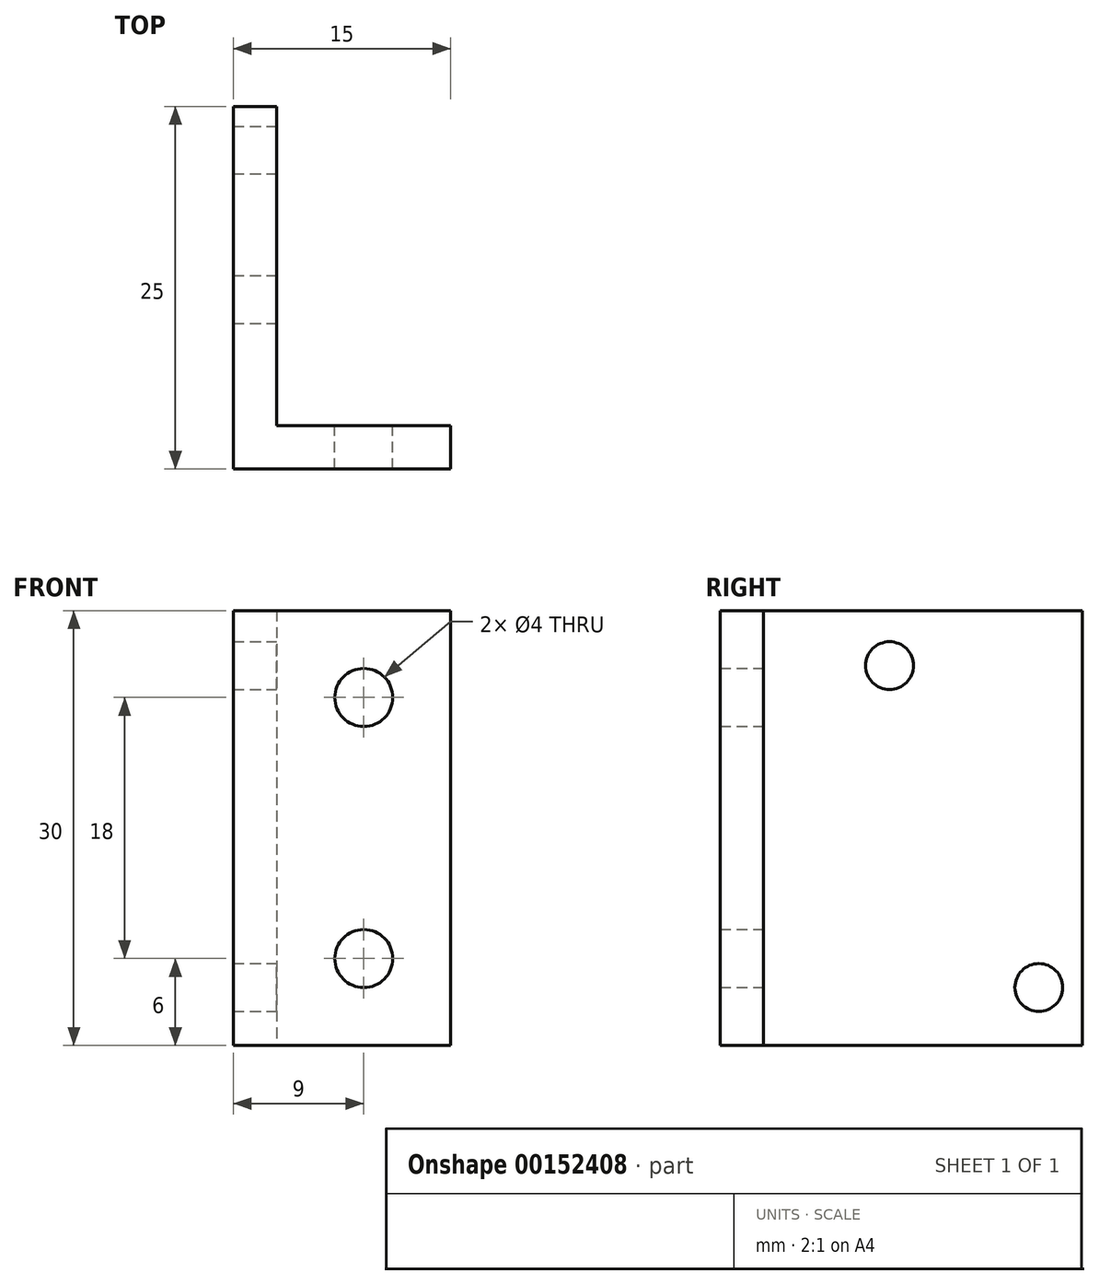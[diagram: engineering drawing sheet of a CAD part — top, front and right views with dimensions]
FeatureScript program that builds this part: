
annotation { "Feature Type Name" : "Feature", "Feature Type Description" : "" }
export const myFeature = defineFeature(function(context is Context, id is Id, definition is map)
    precondition{}
    {
        {
            var Q0;
            Q0=qCreatedBy(makeId("Top.planeOp"),FACE);
            var sketch = newSketch(context, id + "F0", { "sketchPlane" : qUnion([Q0])});
            skLineSegment(sketch, "E0", {"start": v(0, 0) * mm, "end": v(15, 0) * mm});
            skLineSegment(sketch, "E1", {"start": v(15, 0) * mm, "end": v(15, 3) * mm});
            skLineSegment(sketch, "E2", {"start": v(15, 3) * mm, "end": v(3, 3) * mm});
            skLineSegment(sketch, "E3", {"start": v(3, 3) * mm, "end": v(3, 25) * mm});
            skLineSegment(sketch, "E4", {"start": v(3, 25) * mm, "end": v(0, 25) * mm});
            skLineSegment(sketch, "E5", {"start": v(0, 25) * mm, "end": v(0, 0) * mm});
            skSolve(sketch);
        }
        {
            var Q0;
            Q0 = qSketchRegion(id + "F0", true);
            extrude(context, id + "F1", {"entities" : qUnion([Q0]), "depth" : 30 * mm});
        }
        {
            var Q0;
            Q0=makeQuery(id+"F1.opExtrude","SWEPT_FACE",FACE,{"disambiguationData":[OSD([sQuery(id+"F0.wireOp",EDGE,"E3")])]});
            var sketch = newSketch(context, id + "F2", { "sketchPlane" : qUnion([Q0])});
            skCircle(sketch, "E6", {"center": v(22, 4) * mm, "radius": 1.65 * mm});
            skCircle(sketch, "E7", {"center": v(11.7, 26.2) * mm, "radius": 1.65 * mm});
            skSolve(sketch);
        }
        {
            var Q0;
            Q0 = qSketchRegion(id + "F2", true);
            extrude(context, id + "F3", {"entities" : qUnion([Q0]), "operationType" : NewBodyOperationType.REMOVE, "endBound" : BoundingType.THROUGH_ALL, "oppositeDirection" : true, "depth" : 25 * mm});
        }
        {
            var Q0;
            Q0=makeQuery(id+"F1.opExtrude","SWEPT_FACE",FACE,{"disambiguationData":[OSD([sQuery(id+"F0.wireOp",EDGE,"E2")])]});
            var sketch = newSketch(context, id + "F4", { "sketchPlane" : qUnion([Q0])});
            skCircle(sketch, "E8", {"center": v(-9, 24) * mm, "radius": 2 * mm});
            skCircle(sketch, "E9", {"center": v(-9, 6) * mm, "radius": 2 * mm});
            skSolve(sketch);
        }
        {
            var Q0;
            Q0 = qSketchRegion(id + "F4", true);
            extrude(context, id + "F5", {"entities" : qUnion([Q0]), "operationType" : NewBodyOperationType.REMOVE, "endBound" : BoundingType.THROUGH_ALL, "oppositeDirection" : true, "depth" : 25 * mm});
        }
    });
